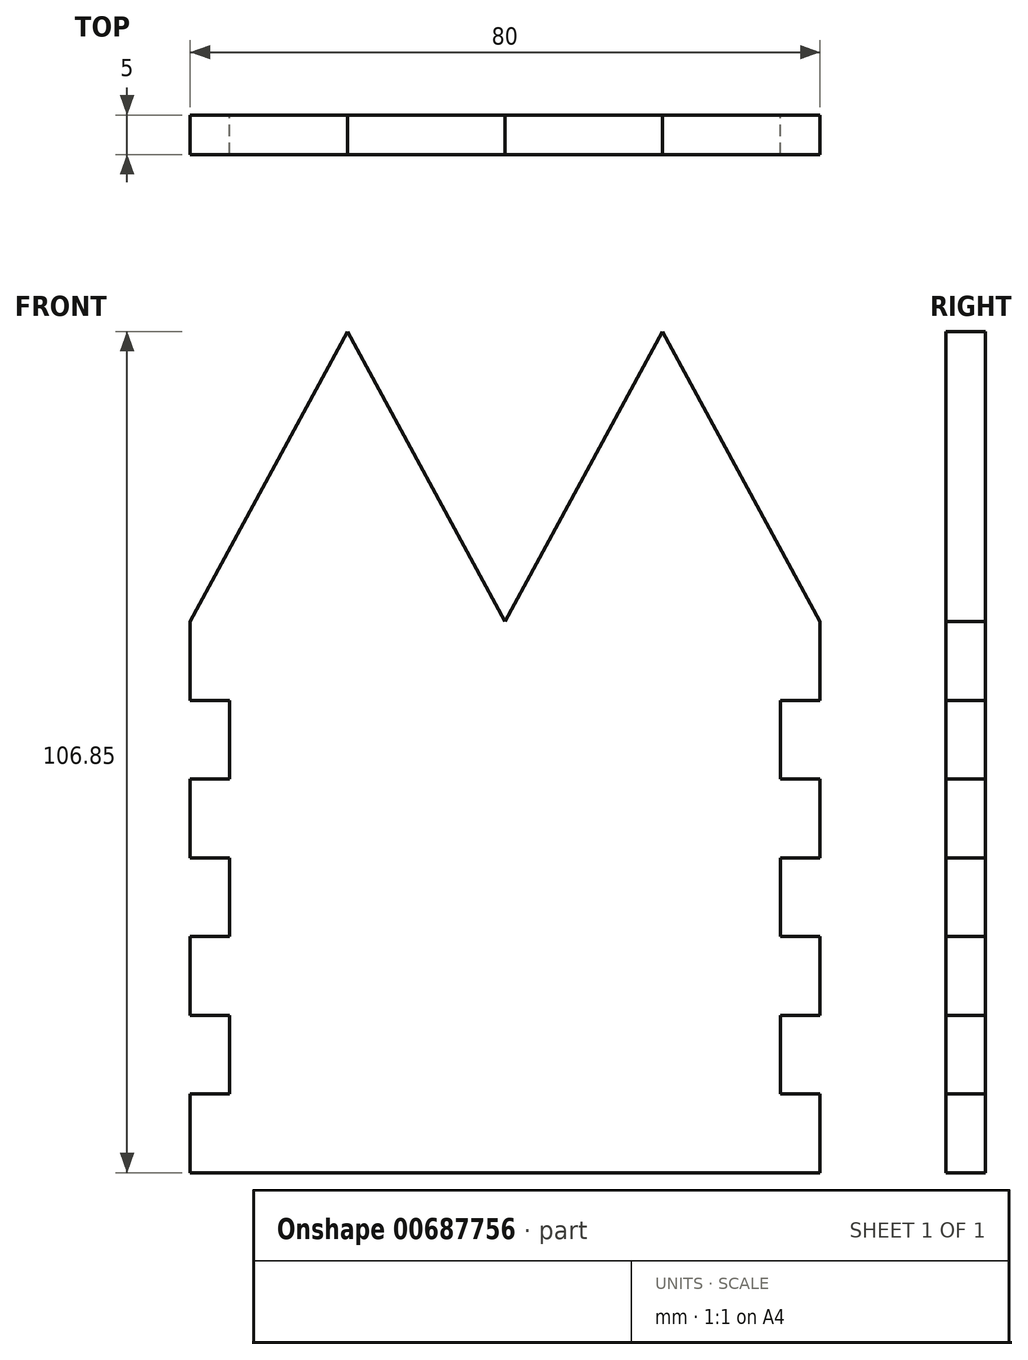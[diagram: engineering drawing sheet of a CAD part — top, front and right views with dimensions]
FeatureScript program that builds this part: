
annotation { "Feature Type Name" : "Feature", "Feature Type Description" : "" }
export const myFeature = defineFeature(function(context is Context, id is Id, definition is map)
    precondition{}
    {
        {
            var Q0;
            Q0=qCreatedBy(makeId("Front.planeOp"),FACE);
            var sketch = newSketch(context, id + "F0", { "sketchPlane" : qUnion([Q0])});
            skLineSegment(sketch, "E0.bottom", {"start": v(-40, 0) * mm, "end": v(0, 0) * mm});
            skLineSegment(sketch, "E0.top", {"start": v(-40, 70) * mm, "end": v(0, 70) * mm});
            skLineSegment(sketch, "E0.left", {"start": v(-40, 0) * mm, "end": v(-40, 10) * mm});
            skLineSegment(sketch, "E0.right", {"start": v(0, 0) * mm, "end": v(0, 70) * mm});
            skLineSegment(sketch, "E1", {"start": v(-20, 106.85) * mm, "end": v(-40, 70) * mm});
            skLineSegment(sketch, "E2", {"start": v(-20, 106.85) * mm, "end": v(0, 70) * mm});
            skPoint(sketch, "E3.start.orphan", {"position": v(-20, 70) * mm});
            skLineSegment(sketch, "E4.bottom", {"start": v(-40, 60) * mm, "end": v(-35, 60) * mm});
            skLineSegment(sketch, "E4.top", {"start": v(-40, 50) * mm, "end": v(-35, 50) * mm});
            skLineSegment(sketch, "E4.right", {"start": v(-35, 60) * mm, "end": v(-35, 50) * mm});
            skLineSegment(sketch, "E5.bottom", {"start": v(-40, 20) * mm, "end": v(-35, 20) * mm});
            skLineSegment(sketch, "E5.top", {"start": v(-40, 10) * mm, "end": v(-35, 10) * mm});
            skLineSegment(sketch, "E5.right", {"start": v(-35, 20) * mm, "end": v(-35, 10) * mm});
            skLineSegment(sketch, "E6.bottom", {"start": v(-35, 40) * mm, "end": v(-40, 40) * mm});
            skLineSegment(sketch, "E6.top", {"start": v(-35, 30) * mm, "end": v(-40, 30) * mm});
            skLineSegment(sketch, "E6.left", {"start": v(-35, 40) * mm, "end": v(-35, 30) * mm});
            skLineSegment(sketch, "E7.trimOffspring", {"start": v(-40, 60) * mm, "end": v(-40, 70) * mm});
            skLineSegment(sketch, "E8.trimOffspring", {"start": v(-40, 40) * mm, "end": v(-40, 50) * mm});
            skLineSegment(sketch, "E9.trimOffspring", {"start": v(-40, 20) * mm, "end": v(-40, 30) * mm});
            skLineSegment(sketch, "E10.MirrorCS", {"start": v(40, 10) * mm, "end": v(35, 10) * mm});
            skLineSegment(sketch, "E11.MirrorCS", {"start": v(35, 30) * mm, "end": v(40, 30) * mm});
            skLineSegment(sketch, "E12.MirrorCS", {"start": v(35, 60) * mm, "end": v(35, 50) * mm});
            skLineSegment(sketch, "E13.MirrorCS", {"start": v(40, 60) * mm, "end": v(40, 70) * mm});
            skLineSegment(sketch, "E14.MirrorCS", {"start": v(40, 50) * mm, "end": v(35, 50) * mm});
            skLineSegment(sketch, "E15.MirrorCS", {"start": v(40, 60) * mm, "end": v(35, 60) * mm});
            skLineSegment(sketch, "E16.MirrorCS", {"start": v(40, 0) * mm, "end": v(40, 10) * mm});
            skLineSegment(sketch, "E17.MirrorCS", {"start": v(40, 40) * mm, "end": v(40, 50) * mm});
            skLineSegment(sketch, "E18.MirrorCS", {"start": v(40, 20) * mm, "end": v(35, 20) * mm});
            skLineSegment(sketch, "E19.MirrorCS", {"start": v(35, 20) * mm, "end": v(35, 10) * mm});
            skLineSegment(sketch, "E20.MirrorCS", {"start": v(40, 20) * mm, "end": v(40, 30) * mm});
            skLineSegment(sketch, "E21.MirrorCS", {"start": v(35, 40) * mm, "end": v(40, 40) * mm});
            skLineSegment(sketch, "E22.MirrorCS", {"start": v(35, 40) * mm, "end": v(35, 30) * mm});
            skLineSegment(sketch, "E23.MirrorCS", {"start": v(40, 70) * mm, "end": v(0, 70) * mm});
            skLineSegment(sketch, "E24.MirrorCS", {"start": v(20, 106.85) * mm, "end": v(40, 70) * mm});
            skPoint(sketch, "E25.MirrorP", {"position": v(20, 70) * mm});
            skLineSegment(sketch, "E26.MirrorCS", {"start": v(40, 0) * mm, "end": v(0, 0) * mm});
            skLineSegment(sketch, "E27.MirrorCS", {"start": v(20, 106.85) * mm, "end": v(0, 70) * mm});
            skSolve(sketch);
        }
        {
            var Q0;
            Q0 = qSketchRegion(id + "F0", true);
            extrude(context, id + "F1", {"entities" : qUnion([Q0]), "depth" : 5 * mm, "offsetDistance" : 25 * mm});
        }
    });
